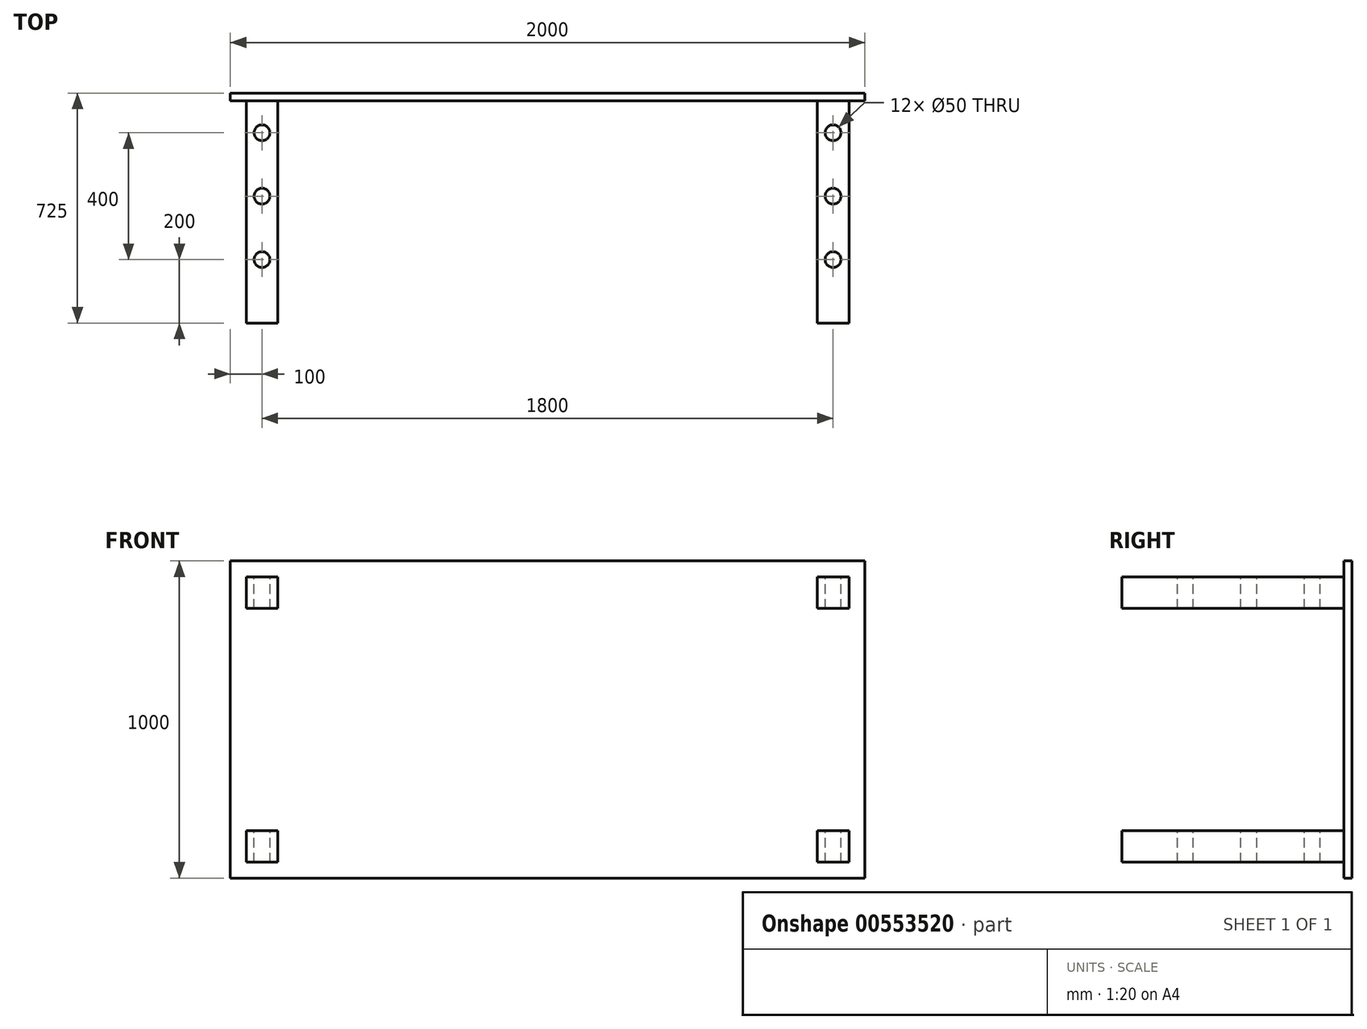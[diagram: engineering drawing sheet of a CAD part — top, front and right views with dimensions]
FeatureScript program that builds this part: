
annotation { "Feature Type Name" : "Feature", "Feature Type Description" : "" }
export const myFeature = defineFeature(function(context is Context, id is Id, definition is map)
    precondition{}
    {
        {
            var Q0;
            Q0=qCreatedBy(makeId("Front.planeOp"),FACE);
            var sketch = newSketch(context, id + "F0", { "sketchPlane" : qUnion([Q0])});
            skLineSegment(sketch, "E0.bottom", {"start": v(-999.85, 441.8) * mm, "end": v(1000.15, 441.8) * mm});
            skLineSegment(sketch, "E0.top", {"start": v(-999.85, -558.2) * mm, "end": v(1000.15, -558.2) * mm});
            skLineSegment(sketch, "E0.left", {"start": v(-999.85, 441.8) * mm, "end": v(-999.85, -558.2) * mm});
            skLineSegment(sketch, "E0.right", {"start": v(1000.15, 441.8) * mm, "end": v(1000.15, -558.2) * mm});
            skSolve(sketch);
        }
        {
            var Q0;
            Q0 = qSketchRegion(id + "F0", true);
            extrude(context, id + "F1", {"entities" : qUnion([Q0]), "depth" : 25 * mm, "offsetDistance" : 25 * mm});
        }
        {
            var Q0;
            Q0=qCreatedBy(makeId("Front.planeOp"),FACE);
            var sketch = newSketch(context, id + "F2", { "sketchPlane" : qUnion([Q0])});
            skLineSegment(sketch, "E1.bottom", {"start": v(-849.85, -408.2) * mm, "end": v(-949.85, -408.2) * mm});
            skLineSegment(sketch, "E1.top", {"start": v(-849.85, -508.2) * mm, "end": v(-949.85, -508.2) * mm});
            skLineSegment(sketch, "E1.left", {"start": v(-849.85, -408.2) * mm, "end": v(-849.85, -508.2) * mm});
            skLineSegment(sketch, "E1.right", {"start": v(-949.85, -408.2) * mm, "end": v(-949.85, -508.2) * mm});
            skPoint(sketch, "E1.middle", {"position": v(-899.85, -458.2) * mm});
            skLineSegment(sketch, "E2.bottom", {"start": v(-849.85, 391.8) * mm, "end": v(-949.85, 391.8) * mm});
            skLineSegment(sketch, "E2.top", {"start": v(-849.85, 291.8) * mm, "end": v(-949.85, 291.8) * mm});
            skLineSegment(sketch, "E2.left", {"start": v(-849.85, 391.8) * mm, "end": v(-849.85, 291.8) * mm});
            skLineSegment(sketch, "E2.right", {"start": v(-949.85, 391.8) * mm, "end": v(-949.85, 291.8) * mm});
            skPoint(sketch, "E2.middle", {"position": v(-899.85, 341.8) * mm});
            skLineSegment(sketch, "E3.bottom", {"start": v(850.15, 391.8) * mm, "end": v(950.15, 391.8) * mm});
            skLineSegment(sketch, "E3.top", {"start": v(850.15, 291.8) * mm, "end": v(950.15, 291.8) * mm});
            skLineSegment(sketch, "E3.left", {"start": v(850.15, 391.8) * mm, "end": v(850.15, 291.8) * mm});
            skLineSegment(sketch, "E3.right", {"start": v(950.15, 391.8) * mm, "end": v(950.15, 291.8) * mm});
            skPoint(sketch, "E3.middle", {"position": v(900.15, 341.8) * mm});
            skLineSegment(sketch, "E4.bottom", {"start": v(850.15, -408.2) * mm, "end": v(950.15, -408.2) * mm});
            skLineSegment(sketch, "E4.top", {"start": v(850.15, -508.2) * mm, "end": v(950.15, -508.2) * mm});
            skLineSegment(sketch, "E4.left", {"start": v(850.15, -408.2) * mm, "end": v(850.15, -508.2) * mm});
            skLineSegment(sketch, "E4.right", {"start": v(950.15, -408.2) * mm, "end": v(950.15, -508.2) * mm});
            skPoint(sketch, "E4.middle", {"position": v(900.15, -458.2) * mm});
            skSolve(sketch);
        }
        {
            var Q0;
            Q0 = qSketchRegion(id + "F2", true);
            extrude(context, id + "F3", {"entities" : qUnion([Q0]), "operationType" : NewBodyOperationType.ADD, "depth" : 725 * mm, "offsetDistance" : 25 * mm});
        }
        {
            var Q0;
            Q0=qCreatedBy(makeId("Top.planeOp"),FACE);
            var sketch = newSketch(context, id + "F4", { "sketchPlane" : qUnion([Q0])});
            skCircle(sketch, "E5", {"center": v(-899.85, -125) * mm, "radius": 25 * mm});
            skCircle(sketch, "E6", {"center": v(-899.85, -325) * mm, "radius": 25 * mm});
            skCircle(sketch, "E7", {"center": v(-899.85, -525) * mm, "radius": 25 * mm});
            skCircle(sketch, "E8", {"center": v(900.15, -525) * mm, "radius": 25 * mm});
            skCircle(sketch, "E9", {"center": v(900.15, -325) * mm, "radius": 25 * mm});
            skCircle(sketch, "E10", {"center": v(900.15, -125) * mm, "radius": 25 * mm});
            skSolve(sketch);
        }
        {
            var Q0;
            Q0 = qSketchRegion(id + "F4", true);
            extrude(context, id + "F5", {"entities" : qUnion([Q0]), "operationType" : NewBodyOperationType.REMOVE, "endBound" : BoundingType.THROUGH_ALL, "oppositeDirection" : true, "depth" : 25 * mm, "offsetDistance" : 25 * mm});
        }
        {
            var Q0;
            Q0=makeQuery(id+"F3.opExtrude","SWEPT_FACE",FACE,{"disambiguationData":[OSD([sQuery(id+"F2.wireOp",EDGE,"E2.bottom")])]});
            var sketch = newSketch(context, id + "F6", { "sketchPlane" : qUnion([Q0])});
            skCircle(sketch, "E11", {"center": v(900.15, -525) * mm, "radius": 25 * mm});
            skCircle(sketch, "E12", {"center": v(900.15, -325) * mm, "radius": 25 * mm});
            skCircle(sketch, "E13", {"center": v(900.15, -125) * mm, "radius": 25 * mm});
            skCircle(sketch, "E14", {"center": v(-899.85, -525) * mm, "radius": 25 * mm});
            skCircle(sketch, "E15", {"center": v(-899.85, -325) * mm, "radius": 25 * mm});
            skCircle(sketch, "E16", {"center": v(-899.85, -125) * mm, "radius": 25 * mm});
            skSolve(sketch);
        }
        {
            var Q0;
            Q0 = qSketchRegion(id + "F6", true);
            extrude(context, id + "F7", {"entities" : qUnion([Q0]), "operationType" : NewBodyOperationType.REMOVE, "endBound" : BoundingType.THROUGH_ALL, "oppositeDirection" : true, "depth" : 25 * mm, "offsetDistance" : 25 * mm});
        }
    });
